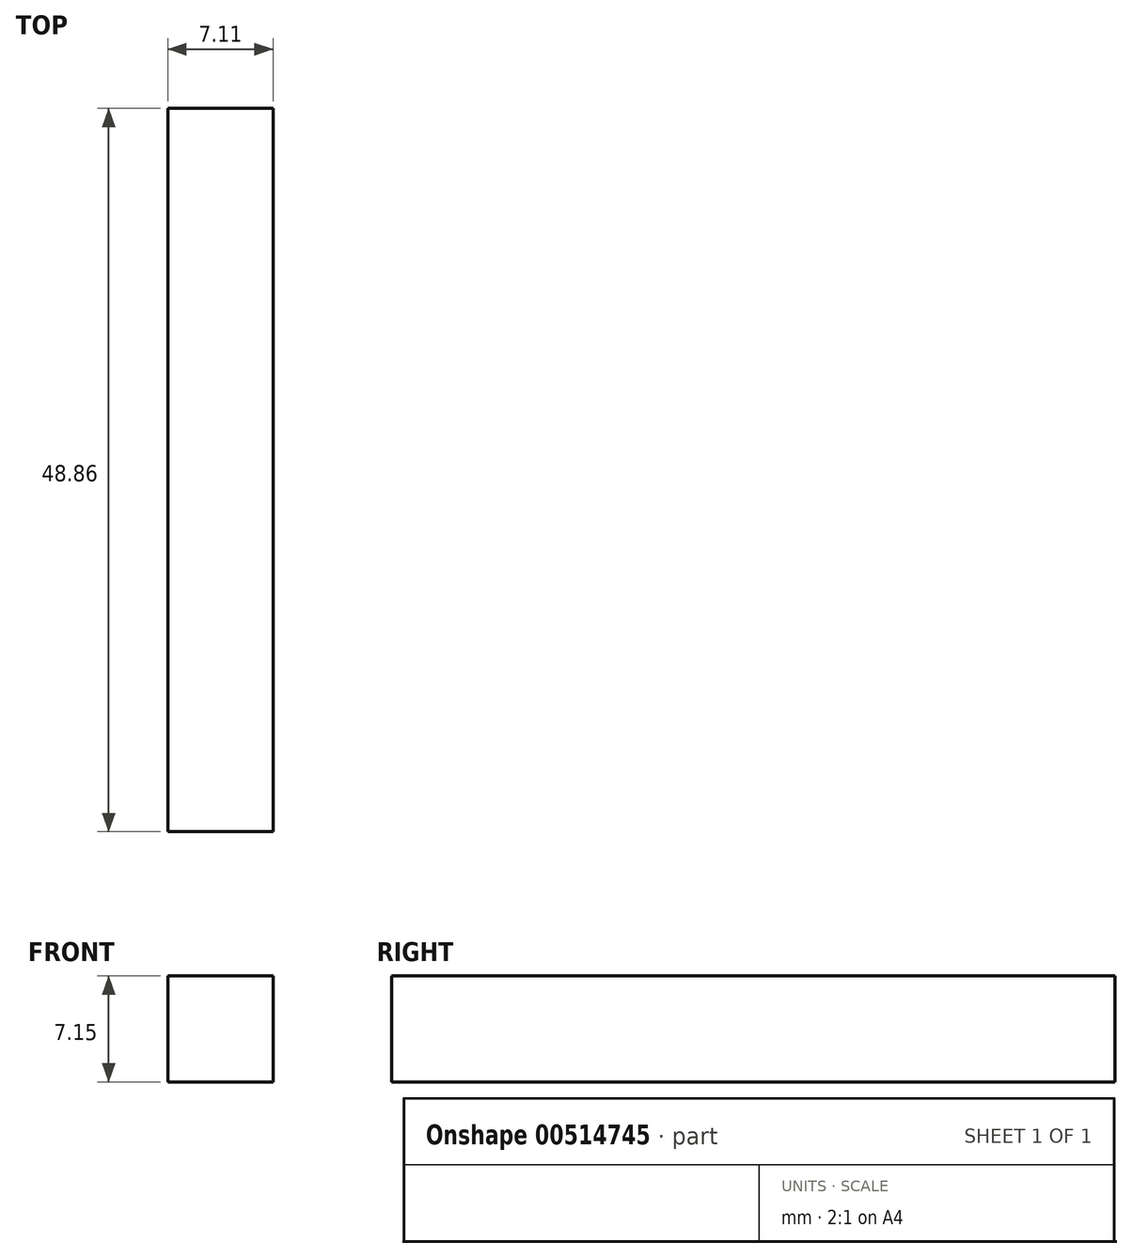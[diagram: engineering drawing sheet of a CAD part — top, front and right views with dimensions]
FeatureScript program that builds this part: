
annotation { "Feature Type Name" : "Feature", "Feature Type Description" : "" }
export const myFeature = defineFeature(function(context is Context, id is Id, definition is map)
    precondition{}
    {
        {
            var Q0;
            Q0=qCreatedBy(makeId("Right.planeOp"),FACE);
            var sketch = newSketch(context, id + "F0", { "sketchPlane" : qUnion([Q0])});
            skLineSegment(sketch, "E0.bottom", {"start": v(48.86, 0) * mm, "end": v(0, 0) * mm});
            skLineSegment(sketch, "E0.top", {"start": v(48.86, 7.15) * mm, "end": v(0, 7.15) * mm});
            skLineSegment(sketch, "E0.left", {"start": v(48.86, 0) * mm, "end": v(48.86, 7.15) * mm});
            skLineSegment(sketch, "E0.right", {"start": v(0, 0) * mm, "end": v(0, 7.15) * mm});
            skSolve(sketch);
        }
        {
            var Q0;
            Q0 = qSketchRegion(id + "F0", true);
            extrude(context, id + "F1", {"entities" : qUnion([Q0]), "depth" : 7.11 * mm, "offsetDistance" : 25.4 * mm});
        }
    });
